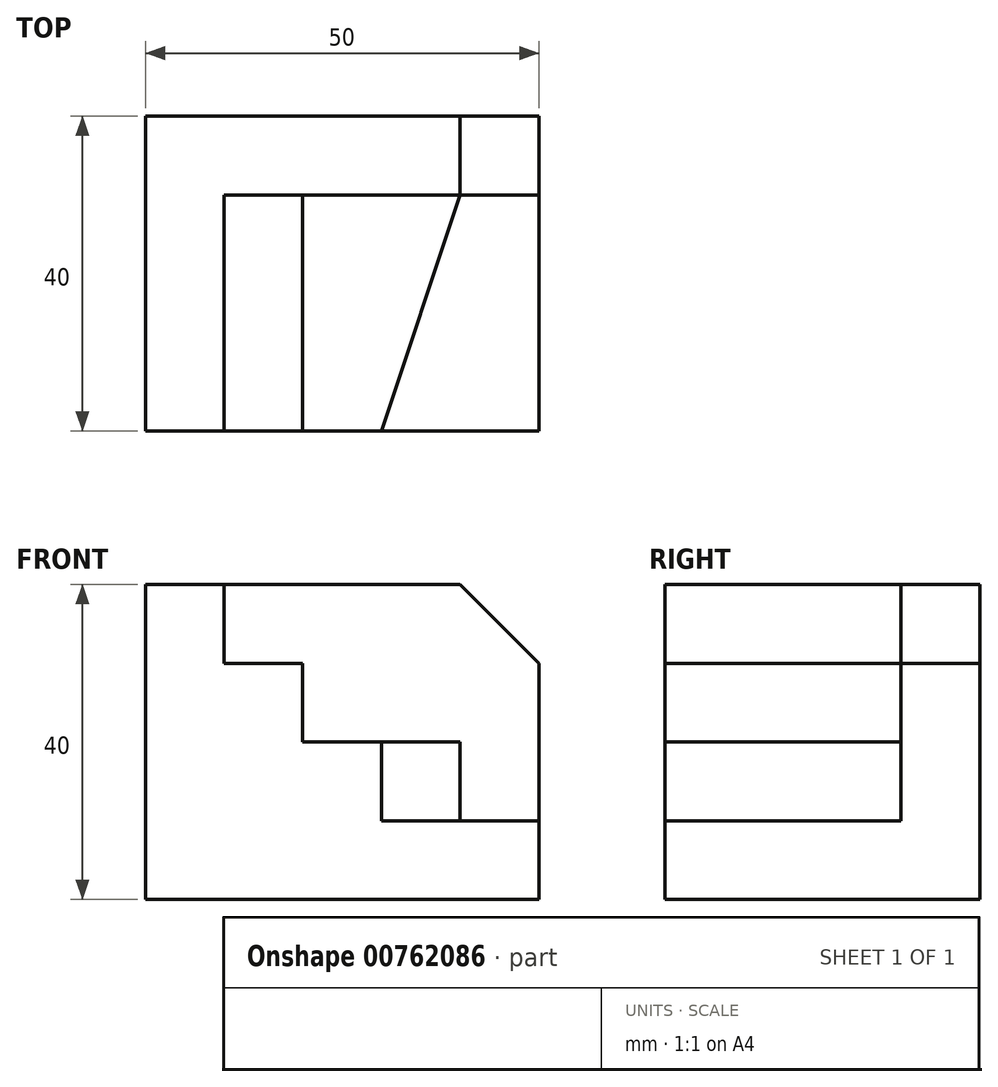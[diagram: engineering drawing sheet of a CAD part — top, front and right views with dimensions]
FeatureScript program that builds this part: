
annotation { "Feature Type Name" : "Feature", "Feature Type Description" : "" }
export const myFeature = defineFeature(function(context is Context, id is Id, definition is map)
    precondition{}
    {
        {
            var Q0;
            Q0=qCreatedBy(makeId("Top.planeOp"),FACE);
            var sketch = newSketch(context, id + "F0", { "sketchPlane" : qUnion([Q0])});
            skLineSegment(sketch, "E0.bottom", {"start": v(0, 0) * mm, "end": v(50, 0) * mm});
            skLineSegment(sketch, "E0.top", {"start": v(0, 40) * mm, "end": v(50, 40) * mm});
            skLineSegment(sketch, "E0.left", {"start": v(0, 0) * mm, "end": v(0, 40) * mm});
            skLineSegment(sketch, "E0.right", {"start": v(50, 0) * mm, "end": v(50, 40) * mm});
            skLineSegment(sketch, "E1", {"start": v(10, 0) * mm, "end": v(10, 30) * mm});
            skLineSegment(sketch, "E2", {"start": v(10, 30) * mm, "end": v(50, 30) * mm});
            skLineSegment(sketch, "E3", {"start": v(20, 30) * mm, "end": v(20, 0) * mm});
            skLineSegment(sketch, "E4", {"start": v(40, 30) * mm, "end": v(30, 0) * mm});
            skSolve(sketch);
        }
        {
            var Q0;
            {var subQ1=sQuery(id+"F0.wireOp",EDGE,"E0.top");Q0=makeQuery(id+"F0.imprint","IMPRINT",FACE,{"disambiguationData":[TD([[makeQuery(id+"F0.imprint","IMPRINT",EDGE,{"derivedFrom":subQ1}),-1.0]])]});}
            extrude(context, id + "F1", {"entities" : qUnion([Q0]), "flatOperationType" : FlatOperationType.REMOVE, "depth" : 40 * mm, "offsetDistance" : 25 * mm, "domain" : OperationDomain.MODEL});
        }
        {
            var Q0;
            {var subQ0=sQuery(id+"F0.wireOp",EDGE,"E1");Q0=makeQuery(id+"F0.imprint","IMPRINT",FACE,{"disambiguationData":[TD([[makeQuery(id+"F0.imprint","IMPRINT",EDGE,{"derivedFrom":subQ0}),-1.0]])]});}
            extrude(context, id + "F2", {"entities" : qUnion([Q0]), "operationType" : NewBodyOperationType.ADD, "depth" : 30 * mm, "offsetDistance" : 25 * mm});
        }
        {
            var Q0;
            {var subQ0=sQuery(id+"F0.wireOp",EDGE,"E3");Q0=makeQuery(id+"F0.imprint","IMPRINT",FACE,{"disambiguationData":[TD([[makeQuery(id+"F0.imprint","IMPRINT",EDGE,{"derivedFrom":subQ0}),1.0]])]});}
            extrude(context, id + "F3", {"entities" : qUnion([Q0]), "operationType" : NewBodyOperationType.ADD, "depth" : 20 * mm, "offsetDistance" : 25 * mm});
        }
        {
            var Q0;
            {var subQ3=sQuery(id+"F0.wireOp",EDGE,"E4");Q0=makeQuery(id+"F0.imprint","IMPRINT",FACE,{"disambiguationData":[TD([[makeQuery(id+"F0.imprint","IMPRINT",EDGE,{"derivedFrom":subQ3}),1.0]])]});}
            extrude(context, id + "F4", {"entities" : qUnion([Q0]), "operationType" : NewBodyOperationType.ADD, "depth" : 10 * mm, "offsetDistance" : 25 * mm});
        }
        {
            var Q0;
            Q0=makeQuery(id+"F1.opExtrude","CAP_EDGE",EDGE,{"disambiguationData":[OSD([sQuery(id+"F0.wireOp",EDGE,"E0.right")])],"isStart":false});
            chamfer(context, id + "F5", {"entities" : qUnion([Q0]), "width" : 10 * mm, "tangentPropagation" : true});
        }
    });
